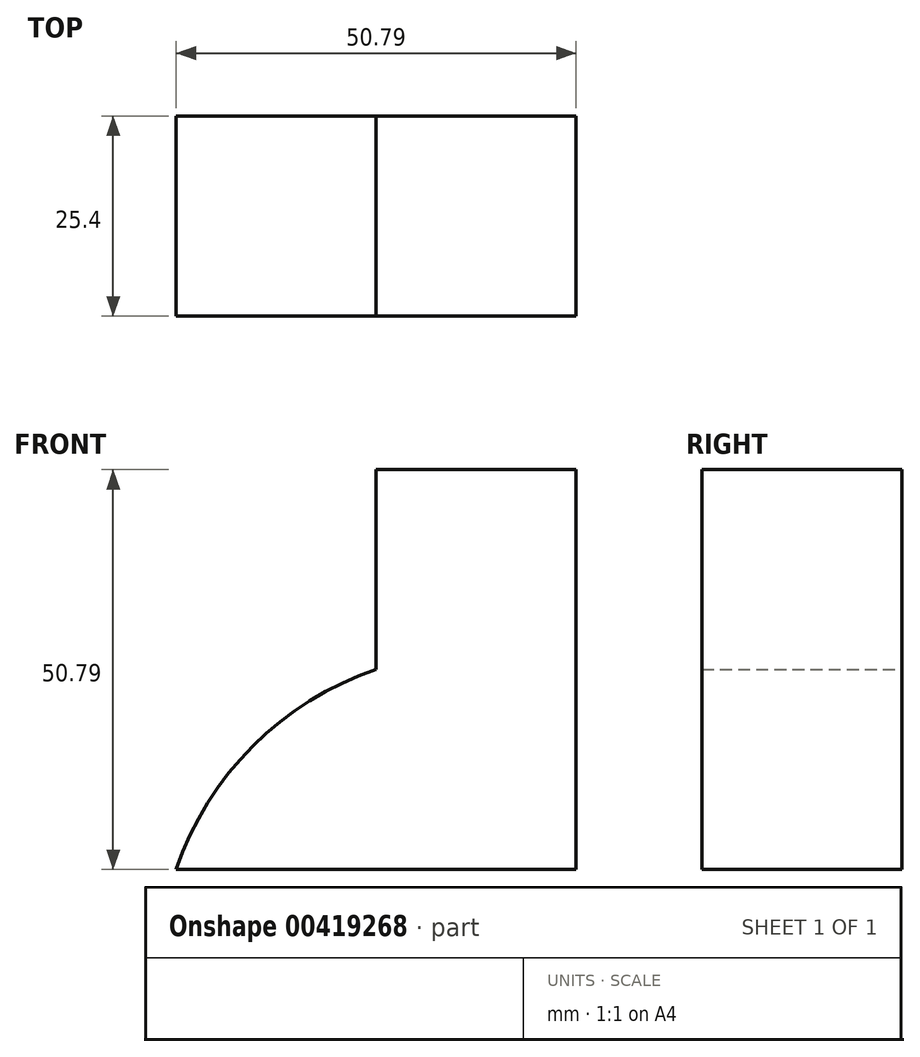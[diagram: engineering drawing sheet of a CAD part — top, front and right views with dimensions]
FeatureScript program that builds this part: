
annotation { "Feature Type Name" : "Feature", "Feature Type Description" : "" }
export const myFeature = defineFeature(function(context is Context, id is Id, definition is map)
    precondition{}
    {
        {
            var Q0;
            Q0=qCreatedBy(makeId("Front.planeOp"),FACE);
            var sketch = newSketch(context, id + "F0", { "sketchPlane" : qUnion([Q0])});
            skLineSegment(sketch, "E0", {"start": v(0, 0) * mm, "end": v(50.8, 0) * mm});
            skLineSegment(sketch, "E1", {"start": v(50.8, 0) * mm, "end": v(50.8, 50.8) * mm});
            skLineSegment(sketch, "E2", {"start": v(50.8, 50.8) * mm, "end": v(25.4, 50.8) * mm});
            skLineSegment(sketch, "E3", {"start": v(25.4, 50.8) * mm, "end": v(25.4, 25.4) * mm});
            skArc(sketch, "E4", {"start": v(25.4, 25.4) * mm, "mid": v(9.73, 15.66) * mm, "end": v(0, 0) * mm});
            skSolve(sketch);
        }
        {
            var Q0;
            Q0=makeQuery(id+"F0.imprint","IMPRINT",FACE,{"disambiguationData":[TD([[makeQuery(id+"F0.imprint","IMPRINT",EDGE,{"derivedFrom":sQuery(id+"F0.wireOp",EDGE,"E0")}),1.0]])]});
            extrude(context, id + "F1", {"entities" : qUnion([Q0]), "depth" : 25.4 * mm});
        }
    });
